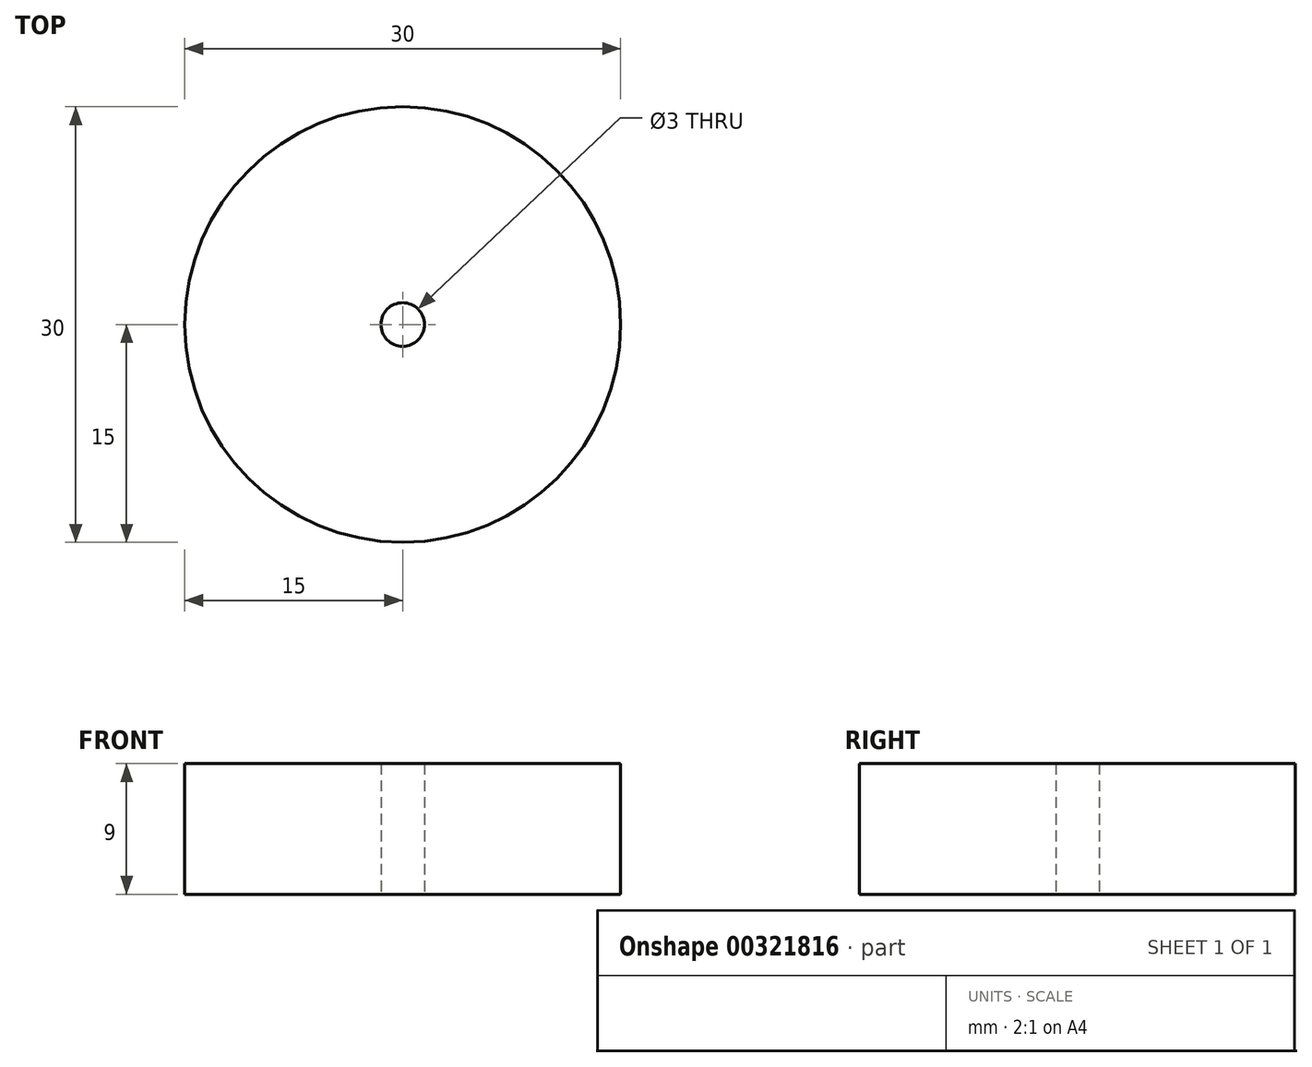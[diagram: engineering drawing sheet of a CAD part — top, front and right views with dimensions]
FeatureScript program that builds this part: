
annotation { "Feature Type Name" : "Feature", "Feature Type Description" : "" }
export const myFeature = defineFeature(function(context is Context, id is Id, definition is map)
    precondition{}
    {
        {
            var Q0;
            Q0=qCreatedBy(makeId("Top.planeOp"),FACE);
            var sketch = newSketch(context, id + "F0", { "sketchPlane" : qUnion([Q0])});
            skCircle(sketch, "E0", {"center": v(0, 0) * mm, "radius": 1.5 * mm});
            skCircle(sketch, "E1", {"center": v(0, 0) * mm, "radius": 15 * mm});
            skSolve(sketch);
        }
        {
            var Q0;
            Q0 = qSketchRegion(id + "F0", true);
            extrude(context, id + "F1", {"entities" : qUnion([Q0]), "depth" : 9 * mm});
        }
    });
